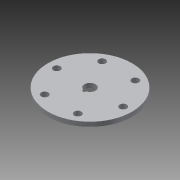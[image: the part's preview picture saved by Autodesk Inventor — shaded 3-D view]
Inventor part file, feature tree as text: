
AUTODESK INVENTOR PART (.ipt)
format: ipt  version: 2014 SP1 (Build 180222100, 222)  size: 100,352 bytes
history: native  units: in
note: dims shown in document units (in); Inventor stores cm internally (conversion verified against a paired STEP export)
features: extrude x1, sketch x1
ambient origin geometry x8: Origin, YZ Plane, XZ Plane, XY Plane, X Axis, Y Axis, Z Axis, Center Point
bodies: Body1 (feature_tree)
feature tree (2):
  extrude  "Extrusion2"  Depth=0.125in
  sketch  "Sketch1"  dims[d0=0.2in d6=0.2in d8=0.2in d10=0.2in d11=2.375in d15=0.315in d19=0.0394in d20=0.0394in d22=0.0in d23=0.0394in d24=0.125in d25=0.0in]
